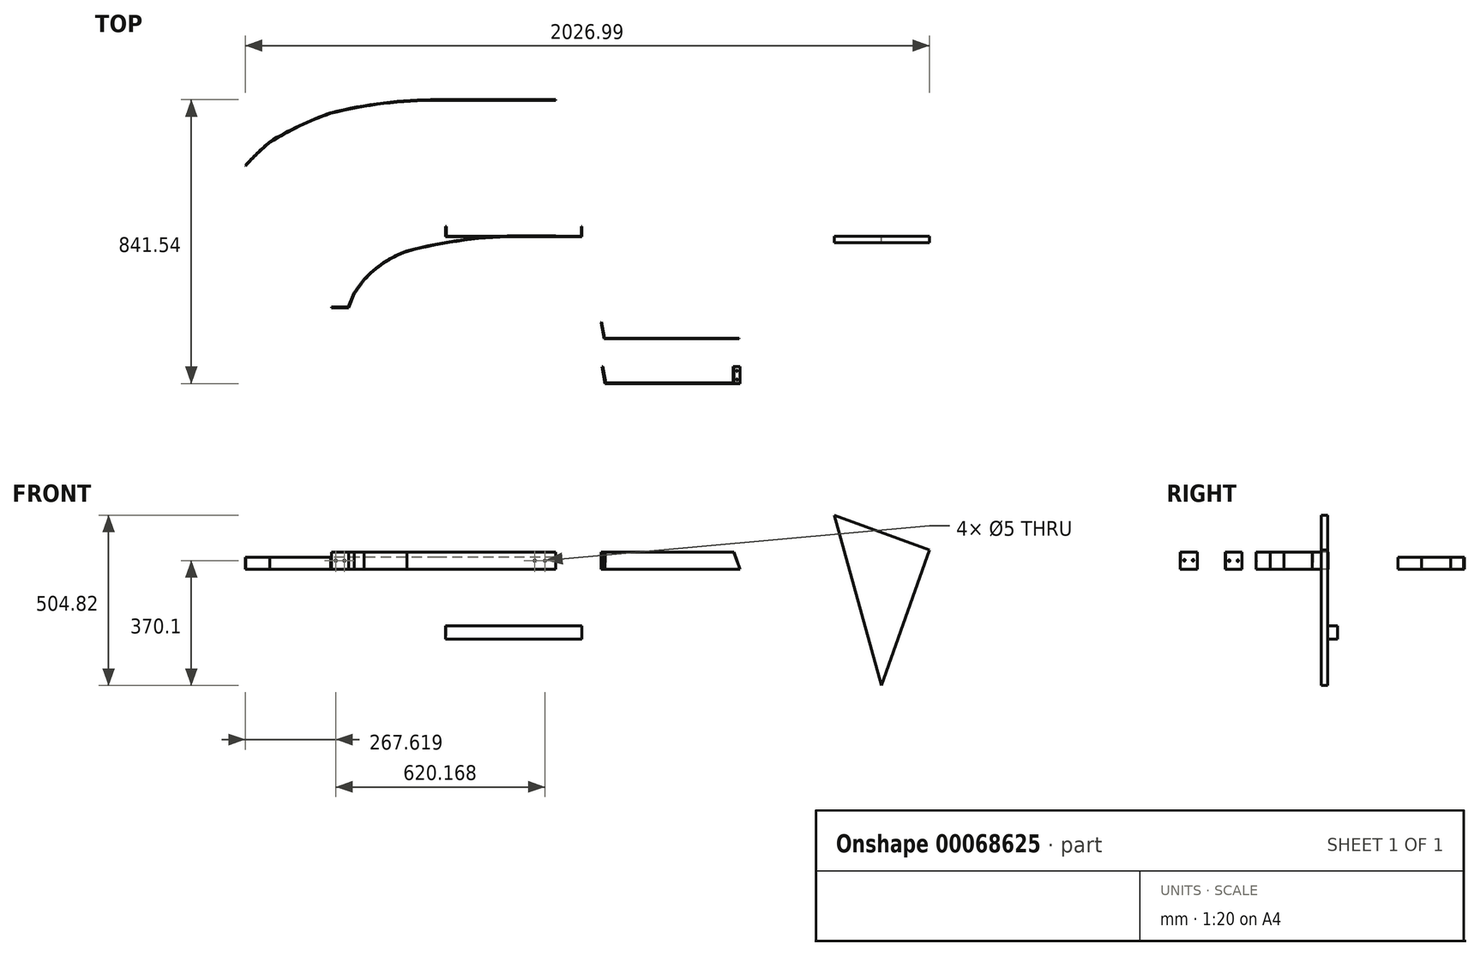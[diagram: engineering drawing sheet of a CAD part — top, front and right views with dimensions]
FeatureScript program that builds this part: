
annotation { "Feature Type Name" : "Feature", "Feature Type Description" : "" }
export const myFeature = defineFeature(function(context is Context, id is Id, definition is map)
    precondition{}
    {
        {
            var Q0;
            Q0=qCreatedBy(makeId("Top.planeOp"),FACE);
            var sketch = newSketch(context, id + "F0", { "sketchPlane" : qUnion([Q0])});
            skPoint(sketch, "E0", {"position": v(0, 0) * mm});
            skPoint(sketch, "E1", {"position": v(-567.57, -130) * mm});
            skPoint(sketch, "E2", {"position": v(-440.66, -45) * mm});
            skArc(sketch, "E3", {"start": v(-440.66, -45) * mm, "mid": v(-509.47, -79.51) * mm, "end": v(-567.57, -130) * mm});
            skPoint(sketch, "E4", {"position": v(-596.93, -170) * mm});
            skPoint(sketch, "E5", {"position": v(-100, 0) * mm});
            skLineSegment(sketch, "E6", {"start": v(-100, 0) * mm, "end": v(0, 0) * mm});
            skArc(sketch, "E7", {"start": v(-100, 0) * mm, "mid": v(-271.81, -11.3) * mm, "end": v(-440.66, -45) * mm});
            skArc(sketch, "E8", {"start": v(-567.57, -130) * mm, "mid": v(-582.7, -149.67) * mm, "end": v(-596.93, -170) * mm});
            skPoint(sketch, "E9", {"position": v(0, 403.26) * mm});
            skPoint(sketch, "E10", {"position": v(-846.98, 278.42) * mm});
            skPoint(sketch, "E11", {"position": v(-666.84, 364.43) * mm});
            skArc(sketch, "E12", {"start": v(-666.84, 364.43) * mm, "mid": v(-759.2, 326.22) * mm, "end": v(-846.98, 278.42) * mm});
            skPoint(sketch, "E13", {"position": v(-918.58, 208.7) * mm});
            skPoint(sketch, "E14", {"position": v(-350, 403.26) * mm});
            skLineSegment(sketch, "E15", {"start": v(-350, 403.26) * mm, "end": v(0, 403.26) * mm});
            skArc(sketch, "E16", {"start": v(-350, 403.26) * mm, "mid": v(-509.6, 393.52) * mm, "end": v(-666.84, 364.43) * mm});
            skArc(sketch, "E17", {"start": v(-846.98, 278.42) * mm, "mid": v(-883.86, 244.67) * mm, "end": v(-918.58, 208.7) * mm});
            skLineSegment(sketch, "E18", {"start": v(-596.93, -170) * mm, "end": v(-614.37, -211.46) * mm});
            skLineSegment(sketch, "E19", {"start": v(-614.37, -211.46) * mm, "end": v(-664.37, -211.46) * mm});
            skLineSegment(sketch, "E20.bottom", {"start": v(0, -1) * mm, "end": v(2, -1) * mm});
            skLineSegment(sketch, "E20.top", {"start": v(0, 49) * mm, "end": v(2, 49) * mm});
            skLineSegment(sketch, "E20.left", {"start": v(0, -1) * mm, "end": v(0, 49) * mm});
            skLineSegment(sketch, "E20.right", {"start": v(2, -1) * mm, "end": v(2, 49) * mm});
            skSolve(sketch);
        }
        {
            var Q0;
            Q0=qCreatedBy(makeId("Right.planeOp"),FACE);
            var sketch = newSketch(context, id + "F1", { "sketchPlane" : qUnion([Q0])});
            skLineSegment(sketch, "E21.bottom", {"start": v(1, 0) * mm, "end": v(-1, 0) * mm});
            skLineSegment(sketch, "E21.top", {"start": v(1, 50) * mm, "end": v(-1, 50) * mm});
            skLineSegment(sketch, "E21.left", {"start": v(1, 0) * mm, "end": v(1, 50) * mm});
            skLineSegment(sketch, "E21.right", {"start": v(-1, 0) * mm, "end": v(-1, 50) * mm});
            skLineSegment(sketch, "E22.bottom", {"start": v(404.26, 0) * mm, "end": v(402.26, 0) * mm});
            skLineSegment(sketch, "E22.top", {"start": v(404.26, 35) * mm, "end": v(402.26, 35) * mm});
            skLineSegment(sketch, "E22.left", {"start": v(404.26, 0) * mm, "end": v(404.26, 35) * mm});
            skLineSegment(sketch, "E22.right", {"start": v(402.26, 0) * mm, "end": v(402.26, 35) * mm});
            skSolve(sketch);
        }
        {
            var Q0;
            Q0=makeQuery(id+"F1.imprint","IMPRINT",FACE,{"disambiguationData":[TD([[makeQuery(id+"F1.imprint","IMPRINT",EDGE,{"derivedFrom":sQuery(id+"F1.wireOp",EDGE,"E21.bottom")}),-1.0]])]});
            var Q1;
            Q1=sQuery(id+"F0.wireOp",EDGE,"E6");
            var Q2;
            Q2=sQuery(id+"F0.wireOp",EDGE,"E7");
            var Q3;
            Q3=sQuery(id+"F0.wireOp",EDGE,"E3");
            var Q4;
            Q4=sQuery(id+"F0.wireOp",EDGE,"E8");
            var Q5;
            Q5=sQuery(id+"F0.wireOp",EDGE,"E18");
            var Q6;
            Q6=sQuery(id+"F0.wireOp",EDGE,"E19");
            sweep(context, id + "F2", {"profiles" : qUnion([Q0]), "path" : qUnion([Q1, Q2, Q3, Q4, Q5, Q6])});
        }
        {
            var Q0;
            Q0=makeQuery(id+"F1.imprint","IMPRINT",FACE,{"disambiguationData":[TD([[makeQuery(id+"F1.imprint","IMPRINT",EDGE,{"derivedFrom":sQuery(id+"F1.wireOp",EDGE,"E22.bottom")}),-1.0]])]});
            var Q1;
            Q1=sQuery(id+"F0.wireOp",EDGE,"E15");
            var Q2;
            Q2=sQuery(id+"F0.wireOp",EDGE,"E16");
            var Q3;
            Q3=sQuery(id+"F0.wireOp",EDGE,"E12");
            var Q4;
            Q4=sQuery(id+"F0.wireOp",EDGE,"E17");
            sweep(context, id + "F3", {"profiles" : qUnion([Q0]), "path" : qUnion([Q1, Q2, Q3, Q4])});
        }
        {
            var Q0;
            Q0=makeQuery(id+"F2.opSweep","SWEPT_FACE",FACE,{"disambiguationData":[OSD([sQuery(id+"F0.wireOp",EDGE,"E19"),sQuery(id+"F1.wireOp",EDGE,"E21.right")])]});
            var sketch = newSketch(context, id + "F4", { "sketchPlane" : qUnion([Q0])});
            skCircle(sketch, "E23", {"center": v(-651.7, 25) * mm, "radius": 2.5 * mm});
            skCircle(sketch, "E24", {"center": v(-625.7, 25) * mm, "radius": 2.5 * mm});
            skSolve(sketch);
        }
        {
            var Q0;
            Q0 = qSketchRegion(id + "F4", true);
            extrude(context, id + "F5", {"entities" : qUnion([Q0]), "operationType" : NewBodyOperationType.REMOVE, "oppositeDirection" : true, "depth" : 3 * mm});
        }
        {
            var Q0;
            Q0=qCreatedBy(makeId("Front.planeOp"),FACE);
            var sketch = newSketch(context, id + "F6", { "sketchPlane" : qUnion([Q0])});
            skLineSegment(sketch, "E25", {"start": v(965.3, -345.1) * mm, "end": v(1107.67, 57.25) * mm});
            skLineSegment(sketch, "E26", {"start": v(1107.67, 57.25) * mm, "end": v(825.71, 159.72) * mm});
            skLineSegment(sketch, "E27", {"start": v(825.71, 159.72) * mm, "end": v(965.3, -345.1) * mm});
            skSolve(sketch);
        }
        {
            var Q0;
            Q0 = qSketchRegion(id + "F6", true);
            extrude(context, id + "F7", {"entities" : qUnion([Q0]), "depth" : 20 * mm});
        }
        {
            var Q0;
            Q0=qCreatedBy(makeId("Front.planeOp"),FACE);
            var sketch = newSketch(context, id + "F8", { "sketchPlane" : qUnion([Q0])});
            skLineSegment(sketch, "E28.bottom", {"start": v(-323.68, -167.52) * mm, "end": v(76.32, -167.52) * mm});
            skLineSegment(sketch, "E28.top", {"start": v(-323.68, -207.52) * mm, "end": v(76.32, -207.52) * mm});
            skLineSegment(sketch, "E28.left", {"start": v(-323.68, -167.52) * mm, "end": v(-323.68, -207.52) * mm});
            skLineSegment(sketch, "E28.right", {"start": v(76.32, -167.52) * mm, "end": v(76.32, -207.52) * mm});
            skSolve(sketch);
        }
        {
            var Q0;
            Q0 = qSketchRegion(id + "F8", true);
            extrude(context, id + "F9", {"entities" : qUnion([Q0]), "depth" : 2 * mm});
        }
        {
            var Q0;
            Q0=makeQuery(id+"F9.opExtrude","CAP_FACE",FACE,{"disambiguationData":[OSD([sQuery(id+"F8.wireOp",EDGE,"E28.bottom"),sQuery(id+"F8.wireOp",EDGE,"E28.top"),sQuery(id+"F8.wireOp",EDGE,"E28.left"),sQuery(id+"F8.wireOp",EDGE,"E28.right")])],"isStart":false});
            var sketch = newSketch(context, id + "F10", { "sketchPlane" : qUnion([Q0])});
            skLineSegment(sketch, "E29.bottom", {"start": v(-323.68, -167.52) * mm, "end": v(-325.68, -167.52) * mm});
            skLineSegment(sketch, "E29.top", {"start": v(-323.68, -207.52) * mm, "end": v(-325.68, -207.52) * mm});
            skLineSegment(sketch, "E29.left", {"start": v(-323.68, -167.52) * mm, "end": v(-323.68, -207.52) * mm});
            skLineSegment(sketch, "E29.right", {"start": v(-325.68, -167.52) * mm, "end": v(-325.68, -207.52) * mm});
            skLineSegment(sketch, "E30.bottom", {"start": v(76.32, -167.52) * mm, "end": v(78.32, -167.52) * mm});
            skLineSegment(sketch, "E30.top", {"start": v(76.32, -207.52) * mm, "end": v(78.32, -207.52) * mm});
            skLineSegment(sketch, "E30.left", {"start": v(76.32, -167.52) * mm, "end": v(76.32, -207.52) * mm});
            skLineSegment(sketch, "E30.right", {"start": v(78.32, -167.52) * mm, "end": v(78.32, -207.52) * mm});
            skSolve(sketch);
        }
        {
            var Q0;
            Q0 = qSketchRegion(id + "F10", true);
            extrude(context, id + "F11", {"entities" : qUnion([Q0]), "operationType" : NewBodyOperationType.ADD, "oppositeDirection" : true, "depth" : 30 * mm});
        }
        {
            var Q0;
            Q0=qCreatedBy(makeId("Top.planeOp"),FACE);
            var sketch = newSketch(context, id + "F12", { "sketchPlane" : qUnion([Q0])});
            skLineSegment(sketch, "E31", {"start": v(134.56, -255.33) * mm, "end": v(143.24, -304.57) * mm});
            skLineSegment(sketch, "E32", {"start": v(143.24, -304.57) * mm, "end": v(543.24, -304.57) * mm});
            skLineSegment(sketch, "E33", {"start": v(134.56, -255.33) * mm, "end": v(136.53, -254.98) * mm});
            skLineSegment(sketch, "E34", {"start": v(136.53, -254.98) * mm, "end": v(144.92, -302.57) * mm});
            skLineSegment(sketch, "E35", {"start": v(144.92, -302.57) * mm, "end": v(543.24, -302.57) * mm});
            skLineSegment(sketch, "E36", {"start": v(543.24, -304.57) * mm, "end": v(543.24, -302.57) * mm});
            skSolve(sketch);
        }
        {
            var Q0;
            Q0 = qSketchRegion(id + "F12", true);
            extrude(context, id + "F13", {"entities" : qUnion([Q0]), "depth" : 50 * mm});
        }
        {
            var Q0;
            Q0=makeQuery(id+"F13.opExtrude","SWEPT_FACE",FACE,{"disambiguationData":[OSD([sQuery(id+"F12.wireOp",EDGE,"E31")])]});
            var sketch = newSketch(context, id + "F14", { "sketchPlane" : qUnion([Q0])});
            skCircle(sketch, "E37", {"center": v(312.81, 25) * mm, "radius": 2.5 * mm});
            skCircle(sketch, "E38", {"center": v(286.81, 25) * mm, "radius": 2.5 * mm});
            skSolve(sketch);
        }
        {
            var Q0;
            Q0 = qSketchRegion(id + "F14", true);
            extrude(context, id + "F15", {"entities" : qUnion([Q0]), "operationType" : NewBodyOperationType.REMOVE, "oppositeDirection" : true, "depth" : 2 * mm});
        }
        {
            var Q0;
            Q0=makeQuery(id+"F13.opExtrude","SWEPT_FACE",FACE,{"disambiguationData":[OSD([sQuery(id+"F12.wireOp",EDGE,"E32")])]});
            var sketch = newSketch(context, id + "F16", { "sketchPlane" : qUnion([Q0])});
            skLineSegment(sketch, "E39", {"start": v(543.24, 0) * mm, "end": v(510.54, 89.84) * mm});
            skLineSegment(sketch, "E40", {"start": v(510.54, 89.84) * mm, "end": v(562.3, 89.84) * mm});
            skLineSegment(sketch, "E41", {"start": v(562.3, 89.84) * mm, "end": v(562.3, 0) * mm});
            skLineSegment(sketch, "E42", {"start": v(562.3, 0) * mm, "end": v(543.24, 0) * mm});
            skSolve(sketch);
        }
        {
            var Q0;
            Q0 = qSketchRegion(id + "F16", true);
            extrude(context, id + "F17", {"entities" : qUnion([Q0]), "operationType" : NewBodyOperationType.REMOVE, "oppositeDirection" : true, "depth" : 25 * mm});
        }
        {
            var Q0;
            Q0=qCreatedBy(makeId("Top.planeOp"),FACE);
            var sketch = newSketch(context, id + "F18", { "sketchPlane" : qUnion([Q0])});
            skLineSegment(sketch, "E43", {"start": v(138.1, -387.28) * mm, "end": v(146.92, -437.28) * mm});
            skLineSegment(sketch, "E44", {"start": v(146.92, -437.28) * mm, "end": v(546.92, -437.28) * mm});
            skLineSegment(sketch, "E45", {"start": v(546.92, -437.28) * mm, "end": v(546.92, -387.28) * mm});
            skLineSegment(sketch, "E46", {"start": v(546.92, -387.28) * mm, "end": v(138.1, -387.28) * mm});
            skSolve(sketch);
        }
        {
            var Q0;
            Q0 = qSketchRegion(id + "F18", true);
            extrude(context, id + "F19", {"entities" : qUnion([Q0]), "depth" : 50 * mm});
        }
        {
            var Q0;
            Q0=makeQuery(id+"F19.opExtrude","SWEPT_FACE",FACE,{"disambiguationData":[OSD([sQuery(id+"F18.wireOp",EDGE,"E44")])]});
            var sketch = newSketch(context, id + "F20", { "sketchPlane" : qUnion([Q0])});
            skLineSegment(sketch, "E47", {"start": v(546.92, 0) * mm, "end": v(528.73, 50) * mm});
            skLineSegment(sketch, "E48", {"start": v(528.73, 50) * mm, "end": v(546.92, 50) * mm});
            skLineSegment(sketch, "E49", {"start": v(546.92, 50) * mm, "end": v(546.92, 0) * mm});
            skSolve(sketch);
        }
        {
            var Q0;
            Q0 = qSketchRegion(id + "F20", true);
            extrude(context, id + "F21", {"entities" : qUnion([Q0]), "operationType" : NewBodyOperationType.REMOVE, "oppositeDirection" : true, "depth" : 50 * mm});
        }
        {
            var Q0;
            Q0=makeQuery(id+"F19.opExtrude","SWEPT_FACE",FACE,{"disambiguationData":[OSD([sQuery(id+"F18.wireOp",EDGE,"E46")])]});
            var Q1;
            Q1=makeQuery(id+"F19.opExtrude","CAP_FACE",FACE,{"disambiguationData":[OSD([sQuery(id+"F18.wireOp",EDGE,"E43"),sQuery(id+"F18.wireOp",EDGE,"E44"),sQuery(id+"F18.wireOp",EDGE,"E45"),sQuery(id+"F18.wireOp",EDGE,"E46")])],"isStart":false});
            var Q2;
            Q2=makeQuery(id+"F19.opExtrude","CAP_FACE",FACE,{"disambiguationData":[OSD([sQuery(id+"F18.wireOp",EDGE,"E43"),sQuery(id+"F18.wireOp",EDGE,"E44"),sQuery(id+"F18.wireOp",EDGE,"E45"),sQuery(id+"F18.wireOp",EDGE,"E46")])],"isStart":true});
            shell(context, id + "F22", {"entities" : qUnion([Q0, Q1, Q2]), "thickness" : 2 * mm});
        }
        {
            var Q0;
            Q0=makeQuery(id+"F19.opExtrude","SWEPT_FACE",FACE,{"disambiguationData":[OSD([sQuery(id+"F18.wireOp",EDGE,"E43")])]});
            var sketch = newSketch(context, id + "F23", { "sketchPlane" : qUnion([Q0])});
            skCircle(sketch, "E50", {"center": v(418.15, 25) * mm, "radius": 2.5 * mm});
            skCircle(sketch, "E51", {"center": v(444.15, 25) * mm, "radius": 2.5 * mm});
            skSolve(sketch);
        }
        {
            var Q0;
            Q0 = qSketchRegion(id + "F23", true);
            extrude(context, id + "F24", {"entities" : qUnion([Q0]), "operationType" : NewBodyOperationType.REMOVE, "oppositeDirection" : true, "depth" : 25 * mm});
        }
        {
            var Q0;
            Q0=makeQuery(id+"F21.boolean.opBoolean","COPY",FACE,{"derivedFrom":makeQuery(id+"F21.opExtrude","SWEPT_FACE",FACE,{"disambiguationData":[OSD([sQuery(id+"F20.wireOp",EDGE,"E47")])]})});
            var sketch = newSketch(context, id + "F25", { "sketchPlane" : qUnion([Q0])});
            skCircle(sketch, "E52", {"center": v(-425.28, -158.85) * mm, "radius": 2.5 * mm});
            skCircle(sketch, "E53", {"center": v(-399.28, -158.85) * mm, "radius": 2.5 * mm});
            skSolve(sketch);
        }
        {
            var Q0;
            Q0 = qSketchRegion(id + "F25", true);
            extrude(context, id + "F26", {"entities" : qUnion([Q0]), "operationType" : NewBodyOperationType.REMOVE, "oppositeDirection" : true, "depth" : 25 * mm});
        }
        {
            var Q0;
            Q0=makeQuery(id+"F2.opSweep","SWEPT_FACE",FACE,{"disambiguationData":[OSD([sQuery(id+"F0.wireOp",EDGE,"E6"),sQuery(id+"F1.wireOp",EDGE,"E21.right")])]});
            var sketch = newSketch(context, id + "F27", { "sketchPlane" : qUnion([Q0])});
            skCircle(sketch, "E54", {"center": v(-61.53, 25) * mm, "radius": 2.5 * mm});
            skCircle(sketch, "E55", {"center": v(-31.53, 25) * mm, "radius": 2.5 * mm});
            skSolve(sketch);
        }
        {
            var Q0;
            Q0 = qSketchRegion(id + "F27", true);
            extrude(context, id + "F28", {"entities" : qUnion([Q0]), "operationType" : NewBodyOperationType.REMOVE, "oppositeDirection" : true, "depth" : 3 * mm});
        }
    });
